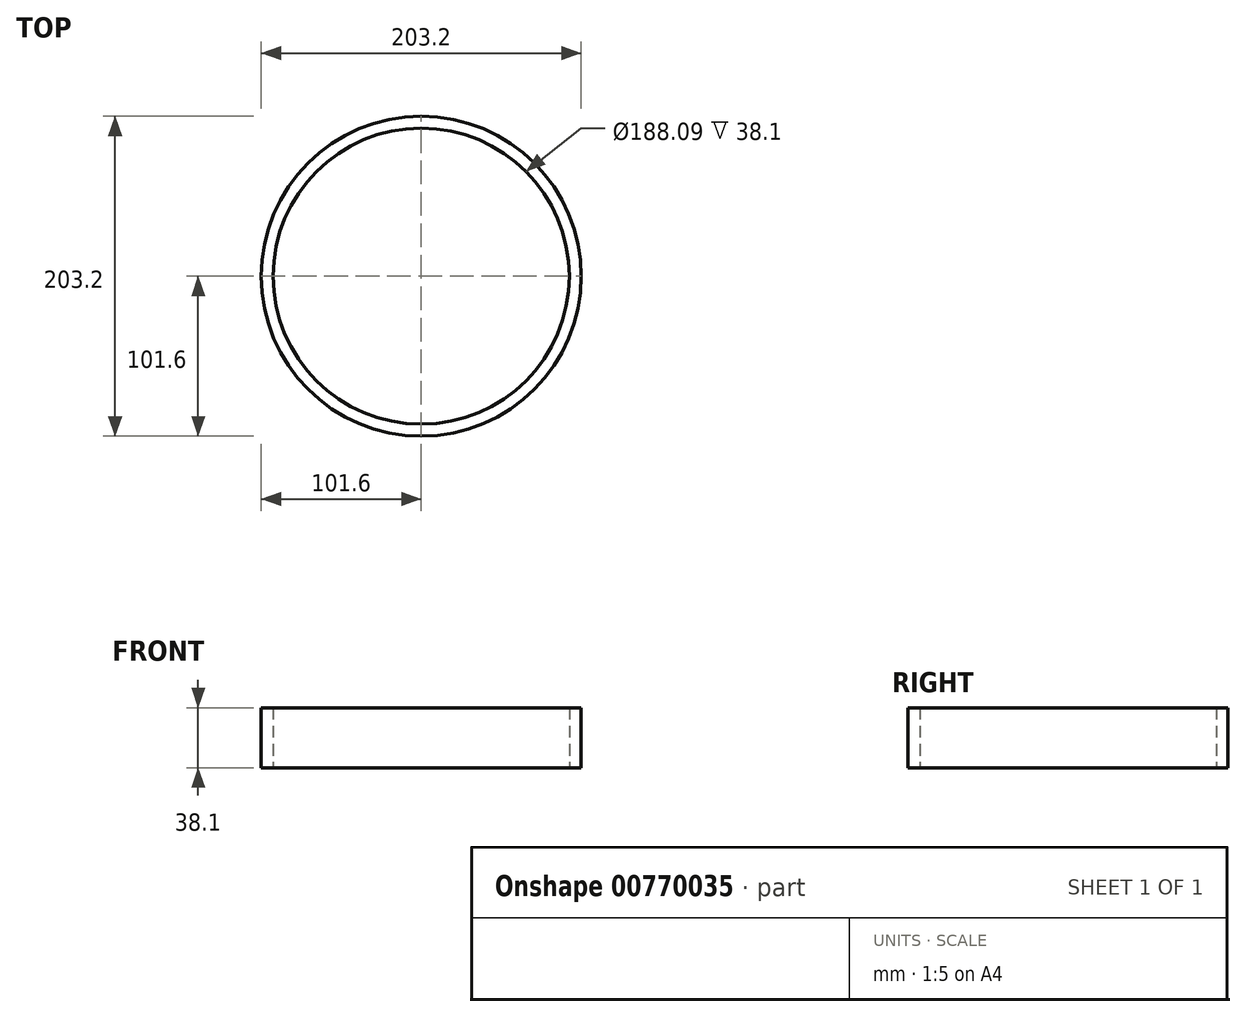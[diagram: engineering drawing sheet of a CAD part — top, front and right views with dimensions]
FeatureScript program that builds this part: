
annotation { "Feature Type Name" : "Feature", "Feature Type Description" : "" }
export const myFeature = defineFeature(function(context is Context, id is Id, definition is map)
    precondition{}
    {
        {
            var Q0;
            Q0=qCreatedBy(makeId("Top.planeOp"),FACE);
            var sketch = newSketch(context, id + "F0", { "sketchPlane" : qUnion([Q0])});
            skCircle(sketch, "E0", {"center": v(0, 0) * mm, "radius": 101.6 * mm});
            skCircle(sketch, "E1", {"center": v(0, 0) * mm, "radius": 94.04 * mm});
            skSolve(sketch);
        }
        {
            var Q0;
            Q0=makeQuery(id+"F0.imprint","IMPRINT",FACE,{"disambiguationData":[TD([[makeQuery(id+"F0.imprint","IMPRINT",EDGE,{"derivedFrom":sQuery(id+"F0.wireOp",EDGE,"E0")}),1.0]])]});
            extrude(context, id + "F1", {"entities" : qUnion([Q0]), "depth" : 38.1 * mm, "offsetDistance" : 25.4 * mm});
        }
    });
